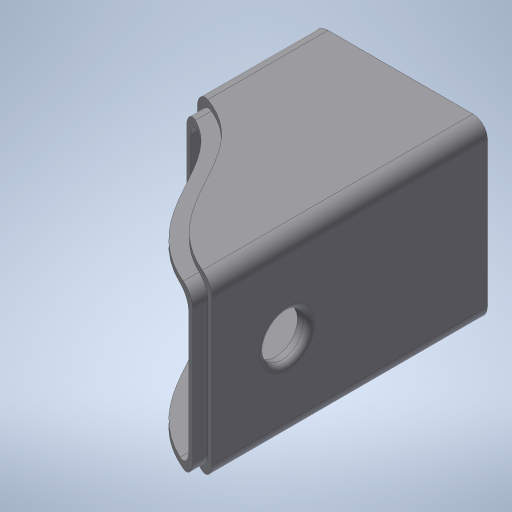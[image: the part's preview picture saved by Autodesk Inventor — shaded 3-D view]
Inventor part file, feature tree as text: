
AUTODESK INVENTOR PART (.ipt)
format: ipt  version: 2023.1 (Build 271208000, 208)  size: 348,672 bytes
history: native  units: mm
features: sketch x5, extrude x4, projected_geometry x3, fillet x2, hole x1
ambient origin geometry x8: Origin, YZ Plane, XZ Plane, XY Plane, X Axis, Y Axis, Z Axis, Center Point
bodies: Solid1 (feature_tree)
feature tree (15):
  extrude  "Extrusion1"  Depth=95.0mm
  extrude  "Extrusion9"  Depth=60.0mm TaperAngle=0.0deg
  extrude  "Extrusion10"  Depth=100.0mm TaperAngle=0.0deg
  extrude  "Extrusion11"  Depth=100.0mm TaperAngle=0.0deg
  hole  "Hole2"  [1 undecoded]
  fillet  "Fillet2"  Radius=5.0mm
  fillet  "Fillet3"  Radius=60.0mm
  sketch  "Sketch1"  dims[d0=60.0mm d1=95.0mm]
  sketch  "Sketch11"  dims[d2=40.0mm d3=60.0mm d4=0.0mm]
  projected_geometry  "Projected Loop8"
  sketch  "Sketch12"  dims[d32=2.0mm d33=100.0mm d34=0.0mm]
  projected_geometry  "Projected Loop9"
  sketch  "Sketch13"  dims[d35=2.0mm d36=100.0mm d37=0.0mm]
  projected_geometry  "Projected Loop10"
  sketch  "Sketch14"  dims[d38=5.0mm d39=5.0mm d40=5.0mm d41=60.0mm d42=0.0mm d43=30.0mm d44=26.0mm d45=15.0mm d46=6.0mm d47=4.0mm d48=2.0mm d49=90.0deg d50=10.0mm d51=20.594885mm d52=2.0mm d53=5.0mm d22=0.5mm d23=0.872665mm d24=0.5mm d25=0.872665mm d30=0.5mm d31=0.872665mm d54=0.375mm d55=0.0mm]
note: 1 required parameter value undecoded (feature->parameter linkage not recoverable at this tier; creation-order binding heuristic only, values carry confidence <= 0.55)
